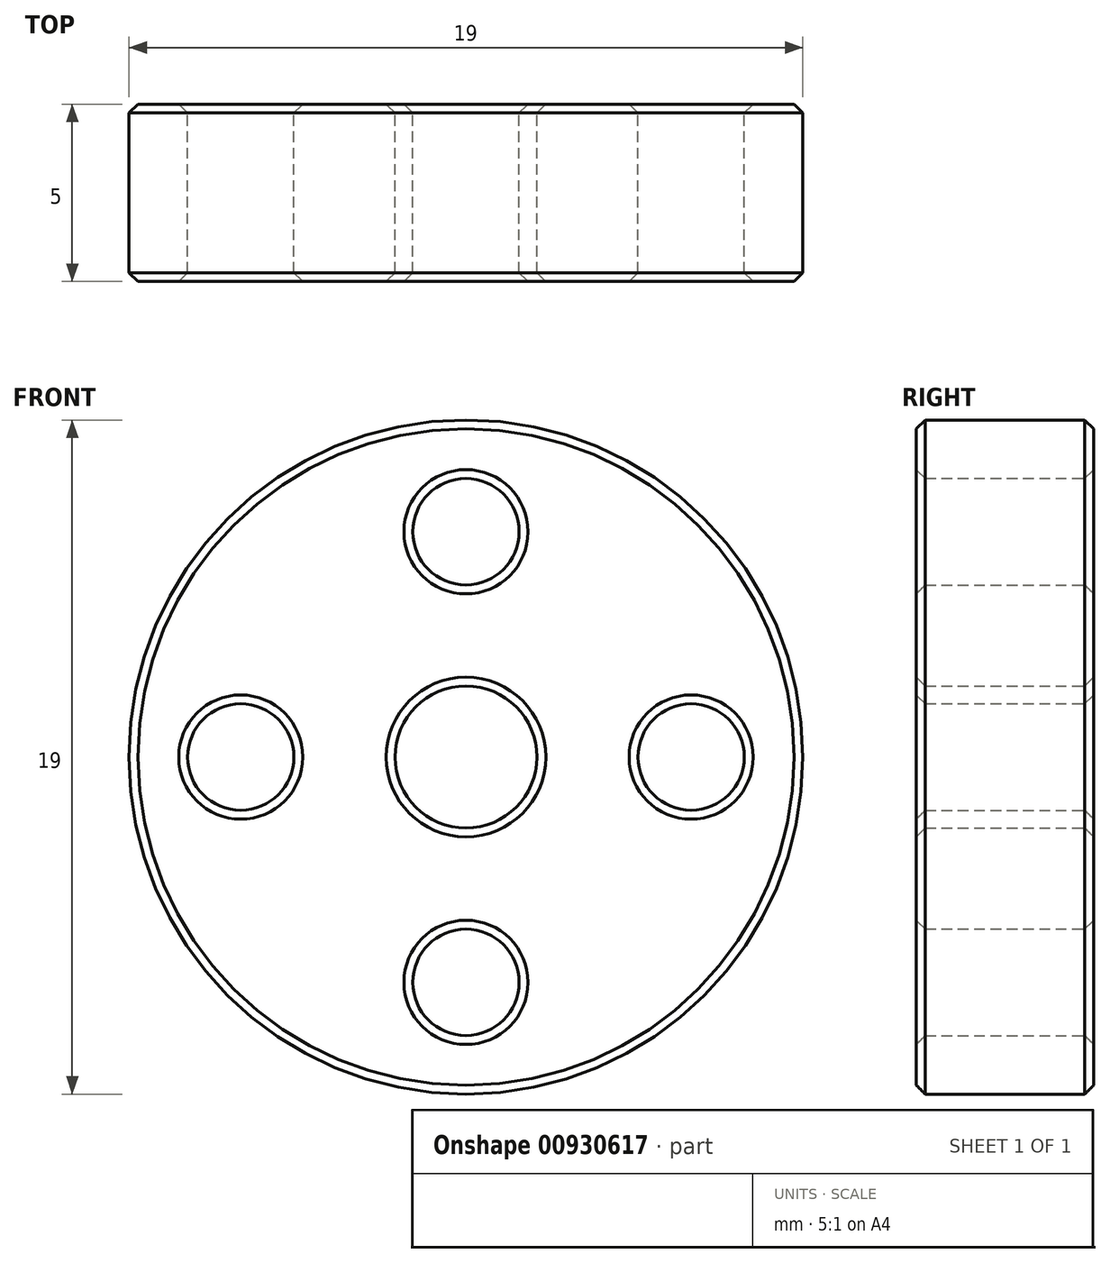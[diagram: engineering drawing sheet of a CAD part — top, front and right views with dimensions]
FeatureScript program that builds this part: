
annotation { "Feature Type Name" : "Feature", "Feature Type Description" : "" }
export const myFeature = defineFeature(function(context is Context, id is Id, definition is map)
    precondition{}
    {
        {
            var Q0;
            Q0=qCreatedBy(makeId("Front.planeOp"),FACE);
            var sketch = newSketch(context, id + "F0", { "sketchPlane" : qUnion([Q0])});
            skCircle(sketch, "E0", {"center": v(0, 0) * mm, "radius": 9.5 * mm});
            skCircle(sketch, "E1", {"center": v(0, 0) * mm, "radius": 2 * mm});
            skCircle(sketch, "E2", {"center": v(0, 6.35) * mm, "radius": 1.5 * mm});
            skCircle(sketch, "E3", {"center": v(0, -6.35) * mm, "radius": 1.5 * mm});
            skCircle(sketch, "E4", {"center": v(6.35, 0) * mm, "radius": 1.5 * mm});
            skCircle(sketch, "E5", {"center": v(-6.35, 0) * mm, "radius": 1.5 * mm});
            skSolve(sketch);
        }
        {
            var Q0;
            Q0=qSketchRegion(id+"F0",true);
            extrude(context, id + "F1", {"entities" : qUnion([Q0]), "depth" : 5 * mm, "offsetDistance" : 25 * mm});
        }
        {
            var Q0;
            Q0=makeQuery(id+"F1.opExtrude","CAP_EDGE",EDGE,{"disambiguationData":[OSD([sQuery(id+"F0.wireOp",EDGE,"E0")])],"isStart":false});
            var Q1;
            Q1=makeQuery(id+"F1.opExtrude","CAP_EDGE",EDGE,{"disambiguationData":[OSD([sQuery(id+"F0.wireOp",EDGE,"E0")])],"isStart":true});
            var Q2;
            Q2=makeQuery(id+"F1.opExtrude","CAP_EDGE",EDGE,{"disambiguationData":[OSD([sQuery(id+"F0.wireOp",EDGE,"E5")])],"isStart":false});
            var Q3;
            Q3=makeQuery(id+"F1.opExtrude","CAP_EDGE",EDGE,{"disambiguationData":[OSD([sQuery(id+"F0.wireOp",EDGE,"E2")])],"isStart":false});
            var Q4;
            Q4=makeQuery(id+"F1.opExtrude","CAP_EDGE",EDGE,{"disambiguationData":[OSD([sQuery(id+"F0.wireOp",EDGE,"E1")])],"isStart":false});
            var Q5;
            Q5=makeQuery(id+"F1.opExtrude","CAP_EDGE",EDGE,{"disambiguationData":[OSD([sQuery(id+"F0.wireOp",EDGE,"E3")])],"isStart":false});
            var Q6;
            Q6=makeQuery(id+"F1.opExtrude","CAP_EDGE",EDGE,{"disambiguationData":[OSD([sQuery(id+"F0.wireOp",EDGE,"E4")])],"isStart":false});
            var Q7;
            Q7=makeQuery(id+"F1.opExtrude","CAP_EDGE",EDGE,{"disambiguationData":[OSD([sQuery(id+"F0.wireOp",EDGE,"E4")])],"isStart":true});
            var Q8;
            Q8=makeQuery(id+"F1.opExtrude","CAP_EDGE",EDGE,{"disambiguationData":[OSD([sQuery(id+"F0.wireOp",EDGE,"E1")])],"isStart":true});
            var Q9;
            Q9=makeQuery(id+"F1.opExtrude","CAP_EDGE",EDGE,{"disambiguationData":[OSD([sQuery(id+"F0.wireOp",EDGE,"E2")])],"isStart":true});
            var Q10;
            Q10=makeQuery(id+"F1.opExtrude","CAP_EDGE",EDGE,{"disambiguationData":[OSD([sQuery(id+"F0.wireOp",EDGE,"E5")])],"isStart":true});
            var Q11;
            Q11=makeQuery(id+"F1.opExtrude","CAP_EDGE",EDGE,{"disambiguationData":[OSD([sQuery(id+"F0.wireOp",EDGE,"E3")])],"isStart":true});
            chamfer(context, id + "F2", {"entities" : qUnion([Q0, Q1, Q2, Q3, Q4, Q5, Q6, Q7, Q8, Q9, Q10, Q11]), "width" : 0.25 * mm, "tangentPropagation" : true});
        }
    });
